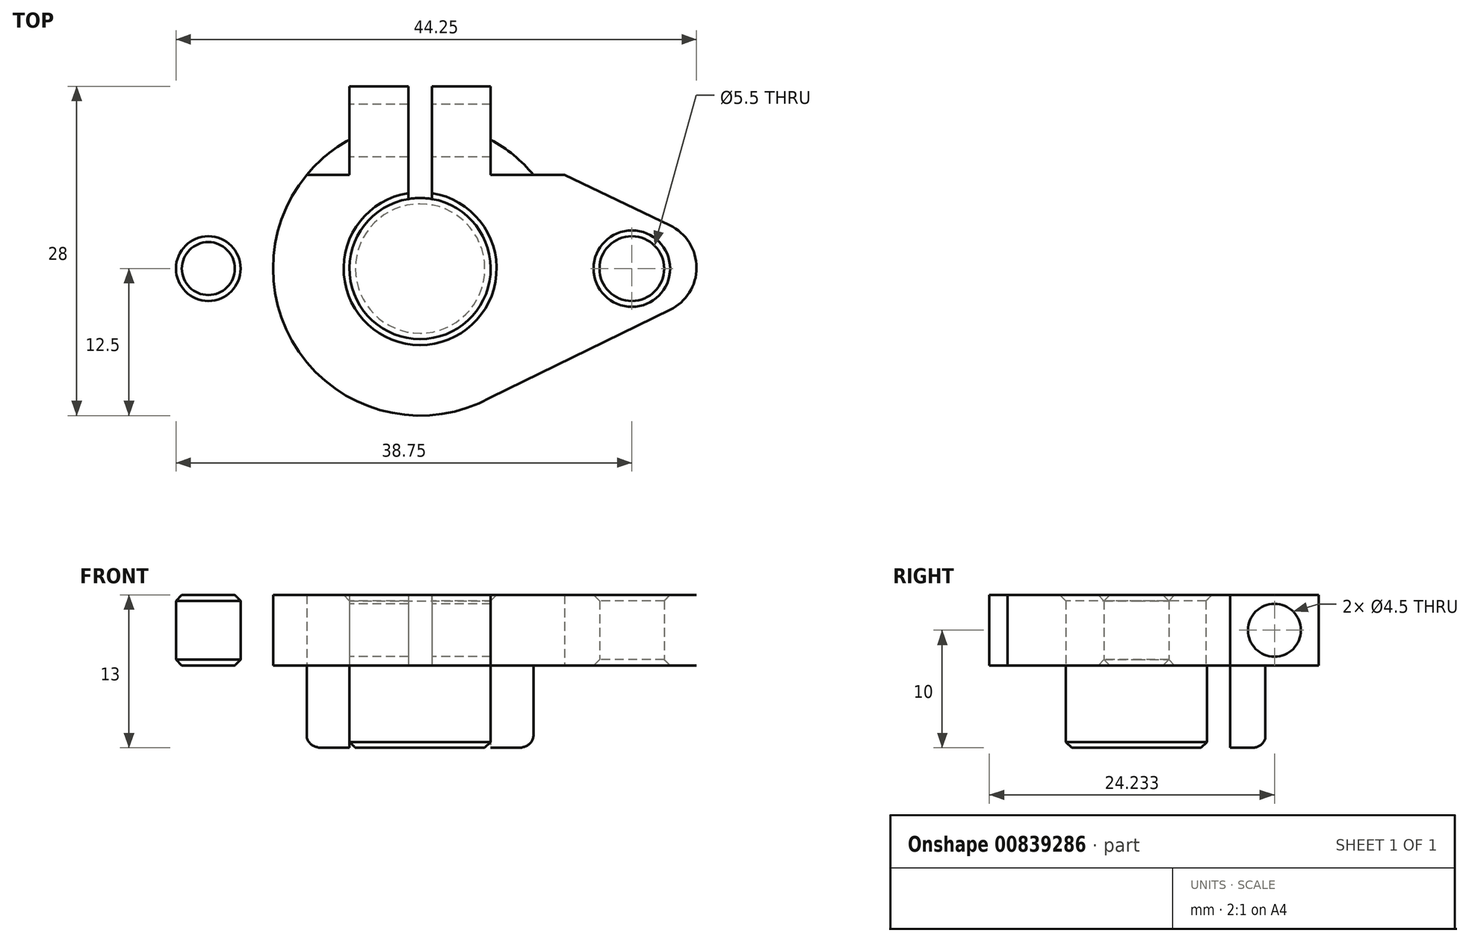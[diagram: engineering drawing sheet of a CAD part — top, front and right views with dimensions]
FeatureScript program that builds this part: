
annotation { "Feature Type Name" : "Feature", "Feature Type Description" : "" }
export const myFeature = defineFeature(function(context is Context, id is Id, definition is map)
    precondition{}
    {
        {
            var Q0;
            Q0=qCreatedBy(makeId("Top.planeOp"),FACE);
            var sketch = newSketch(context, id + "F0", { "sketchPlane" : qUnion([Q0])});
            skCircle(sketch, "E0", {"center": v(0, 0) * mm, "radius": 6 * mm});
            skCircle(sketch, "E1", {"center": v(0, 0) * mm, "radius": 12.5 * mm});
            skCircle(sketch, "E2", {"center": v(18, 0) * mm, "radius": 2.75 * mm});
            skCircle(sketch, "E3.MirrorC", {"center": v(-18, 0) * mm, "radius": 2.75 * mm});
            skLineSegment(sketch, "E4", {"start": v(-1, 5.92) * mm, "end": v(-1, 15.5) * mm});
            skLineSegment(sketch, "E5.MirrorCS", {"start": v(1, 5.92) * mm, "end": v(1, 15.5) * mm});
            skLineSegment(sketch, "E6", {"start": v(-1, 15.5) * mm, "end": v(1, 15.5) * mm});
            skPoint(sketch, "E7", {"position": v(0, -12.5) * mm});
            skLineSegment(sketch, "E8", {"start": v(1, 15.5) * mm, "end": v(6, 15.5) * mm});
            skLineSegment(sketch, "E9", {"start": v(6, 15.5) * mm, "end": v(6, 10.97) * mm});
            skLineSegment(sketch, "E10.MirrorCS", {"start": v(-1, 15.5) * mm, "end": v(-6, 15.5) * mm});
            skLineSegment(sketch, "E11.MirrorCS", {"start": v(-6, 15.5) * mm, "end": v(-6, 10.97) * mm});
            skLineSegment(sketch, "E12", {"start": v(23.5, -2.4) * mm, "end": v(23.5, 2.6) * mm});
            skLineSegment(sketch, "E13.MirrorCS", {"start": v(-23.5, -2.4) * mm, "end": v(-23.5, 2.6) * mm});
            skLineSegment(sketch, "E14", {"start": v(-6, 10.97) * mm, "end": v(-23.5, 2.6) * mm});
            skLineSegment(sketch, "E15", {"start": v(-23.5, -2.4) * mm, "end": v(-6, -10.97) * mm});
            skLineSegment(sketch, "E16", {"start": v(6, -10.97) * mm, "end": v(23.5, -2.4) * mm});
            skLineSegment(sketch, "E17", {"start": v(23.5, 2.6) * mm, "end": v(6, 10.97) * mm});
            skLineSegment(sketch, "E18", {"start": v(6, 10.97) * mm, "end": v(6, 7.97) * mm});
            skLineSegment(sketch, "E19", {"start": v(6, 7.97) * mm, "end": v(12.27, 7.97) * mm});
            skLineSegment(sketch, "E20.MirrorCS", {"start": v(-6, 10.97) * mm, "end": v(-6, 7.97) * mm});
            skLineSegment(sketch, "E21.MirrorCS", {"start": v(-6, 7.97) * mm, "end": v(-12.27, 7.97) * mm});
            skSolve(sketch);
        }
        {
            var Q0;
            Q0=makeQuery(id+"F0.imprint","IMPRINT",FACE,{"disambiguationData":[TD([[makeQuery(id+"F0.imprint","IMPRINT",EDGE,{"derivedFrom":sQuery(id+"F0.wireOp",EDGE,"E3.MirrorC")}),1.0]])]});
            var Q1;
            {var subQ5=sQuery(id+"F0.wireOp",EDGE,"E18");Q1=makeQuery(id+"F0.imprint","IMPRINT",FACE,{"disambiguationData":[TD([[makeQuery(id+"F0.imprint","IMPRINT",EDGE,{"derivedFrom":subQ5}),-1.0]])]});}
            var Q2;
            Q2=makeQuery(id+"F0.imprint","IMPRINT",FACE,{"disambiguationData":[TD([[makeQuery(id+"F0.imprint","IMPRINT",EDGE,{"derivedFrom":sQuery(id+"F0.wireOp",EDGE,"E2")}),-1.0]])]});
            var Q3;
            {var subQ4=sQuery(id+"F0.wireOp",EDGE,"E10.MirrorCS");Q3=makeQuery(id+"F0.imprint","IMPRINT",FACE,{"disambiguationData":[TD([[makeQuery(id+"F0.imprint","IMPRINT",EDGE,{"derivedFrom":subQ4}),1.0]])]});}
            var Q4;
            {var subQ4=sQuery(id+"F0.wireOp",EDGE,"E8");Q4=makeQuery(id+"F0.imprint","IMPRINT",FACE,{"disambiguationData":[TD([[makeQuery(id+"F0.imprint","IMPRINT",EDGE,{"derivedFrom":subQ4}),-1.0]])]});}
            extrude(context, id + "F1", {"entities" : qUnion([Q0, Q1, Q2, Q3, Q4]), "depth" : 6 * mm, "offsetDistance" : 25 * mm});
        }
        {
            var Q0;
            Q0=makeQuery(id+"F1.opExtrude","SWEPT_FACE",FACE,{"disambiguationData":[OSD([sQuery(id+"F0.wireOp",EDGE,"E11.MirrorCS"),sQuery(id+"F0.wireOp",EDGE,"E20.MirrorCS")])]});
            var sketch = newSketch(context, id + "F2", { "sketchPlane" : qUnion([Q0])});
            skLineSegment(sketch, "E22", {"start": v(-15.5, 3) * mm, "end": v(-7.97, 3) * mm});
            skPoint(sketch, "E23", {"position": v(-11.73, 3) * mm});
            skSolve(sketch);
        }
        {
            var Q0;
            Q0=sQuery(id+"F2.wireOp",VERTEX,"E23");
            var Q1;
            Q1=makeQuery(id+"F1.opExtrude","SWEPT_BODY",BODY,{"disambiguationData":[OSD([sQuery(id+"F0.wireOp",EDGE,"E0"),sQuery(id+"F0.wireOp",EDGE,"E1"),sQuery(id+"F0.wireOp",EDGE,"E2"),sQuery(id+"F0.wireOp",EDGE,"E3.MirrorC"),sQuery(id+"F0.wireOp",EDGE,"E4"),sQuery(id+"F0.wireOp",EDGE,"E5.MirrorCS"),sQuery(id+"F0.wireOp",EDGE,"E8"),sQuery(id+"F0.wireOp",EDGE,"E9"),sQuery(id+"F0.wireOp",EDGE,"E10.MirrorCS"),sQuery(id+"F0.wireOp",EDGE,"E11.MirrorCS"),sQuery(id+"F0.wireOp",EDGE,"E12"),sQuery(id+"F0.wireOp",EDGE,"E13.MirrorCS"),sQuery(id+"F0.wireOp",EDGE,"E14"),sQuery(id+"F0.wireOp",EDGE,"E15"),sQuery(id+"F0.wireOp",EDGE,"E16"),sQuery(id+"F0.wireOp",EDGE,"E17"),sQuery(id+"F0.wireOp",EDGE,"E18"),sQuery(id+"F0.wireOp",EDGE,"E19"),sQuery(id+"F0.wireOp",EDGE,"E20.MirrorCS"),sQuery(id+"F0.wireOp",EDGE,"E21.MirrorCS")])]});
            hole(context, id + "F3", {"style" : HoleStyle.SIMPLE, "endStyle" : HoleEndStyle.THROUGH, "standardTappedOrClearance" : lookupTablePath({ "fit" : "Normal", "standard" : "ISO", "size" : "M4", "type" : "Clearance" }), "standardBlindInLast" : lookupTablePath({ "fit" : "Normal", "standard" : "ISO", "engagement" : "75%", "pitch" : "0.7 mm", "size" : "M4", "type" : "Clearance & tapped" }), "holeDiameter" : 4.5 * mm, "majorDiameter" : 3 * mm, "isTappedThrough" : true, "tappedDepth" : 10 * mm, "tapClearance" : 3, "locations" : qUnion([Q0]), "scope" : qUnion([Q1])});
        }
        {
            var Q0;
            Q0=makeQuery(id+"F1.opExtrude","CAP_FACE",FACE,{"disambiguationData":[OSD([sQuery(id+"F0.wireOp",EDGE,"E0"),sQuery(id+"F0.wireOp",EDGE,"E1"),sQuery(id+"F0.wireOp",EDGE,"E2"),sQuery(id+"F0.wireOp",EDGE,"E3.MirrorC"),sQuery(id+"F0.wireOp",EDGE,"E4"),sQuery(id+"F0.wireOp",EDGE,"E5.MirrorCS"),sQuery(id+"F0.wireOp",EDGE,"E8"),sQuery(id+"F0.wireOp",EDGE,"E9"),sQuery(id+"F0.wireOp",EDGE,"E10.MirrorCS"),sQuery(id+"F0.wireOp",EDGE,"E11.MirrorCS"),sQuery(id+"F0.wireOp",EDGE,"E12"),sQuery(id+"F0.wireOp",EDGE,"E13.MirrorCS"),sQuery(id+"F0.wireOp",EDGE,"E14"),sQuery(id+"F0.wireOp",EDGE,"E15"),sQuery(id+"F0.wireOp",EDGE,"E16"),sQuery(id+"F0.wireOp",EDGE,"E17"),sQuery(id+"F0.wireOp",EDGE,"E18"),sQuery(id+"F0.wireOp",EDGE,"E19"),sQuery(id+"F0.wireOp",EDGE,"E20.MirrorCS"),sQuery(id+"F0.wireOp",EDGE,"E21.MirrorCS")])],"isStart":true});
            var sketch = newSketch(context, id + "F4", { "sketchPlane" : qUnion([Q0])});
            skCircle(sketch, "E24", {"center": v(0, 0) * mm, "radius": 6 * mm});
            skCircle(sketch, "E25", {"center": v(0, 0) * mm, "radius": 12.5 * mm});
            skLineSegment(sketch, "E26", {"start": v(1, -5.92) * mm, "end": v(1, -12.46) * mm});
            skLineSegment(sketch, "E27", {"start": v(-1, -5.92) * mm, "end": v(-1, -12.46) * mm});
            skSolve(sketch);
        }
        {
            var Q0;
            Q0=makeQuery(id+"F4.imprint","IMPRINT",FACE,{"disambiguationData":[TD([[makeQuery(id+"F4.imprint","IMPRINT",EDGE,{"disambiguationData":[OD(0.0)],"derivedFrom":sQuery(id+"F4.wireOp",EDGE,"E24")}),1.0]])]});
            var Q1;
            {var subQ0=sQuery(id+"F4.wireOp",EDGE,"E25");var subQ1=makeQuery(id+"F1.opExtrude","CAP_EDGE",EDGE,{"disambiguationData":[OSD([sQuery(id+"F0.wireOp",EDGE,"E9"),sQuery(id+"F0.wireOp",EDGE,"E18")])],"isStart":true});var subQ2=makeQuery(id+"F4.imprint","INTERSECT",VERTEX,{"derivedFrom":[subQ1,subQ0]});var subQ3=makeQuery(id+"F1.opExtrude","CAP_EDGE",EDGE,{"disambiguationData":[OSD([sQuery(id+"F0.wireOp",EDGE,"E19")])],"isStart":true});var subQ4=makeQuery(id+"F4.imprint","INTERSECT",VERTEX,{"derivedFrom":[subQ3,subQ0]});Q1=makeQuery(id+"F4.imprint","IMPRINT",FACE,{"disambiguationData":[TD([[makeQuery(id+"F4.imprint","IMPRINT",EDGE,{"disambiguationData":[TD([[subQ2,-1.0],[subQ4,1.0]])],"derivedFrom":subQ0}),1.0]])]});}
            var Q2;
            {var subQ0=sQuery(id+"F4.wireOp",EDGE,"E25");var subQ1=makeQuery(id+"F1.opExtrude","CAP_EDGE",EDGE,{"disambiguationData":[OSD([sQuery(id+"F0.wireOp",EDGE,"E21.MirrorCS")])],"isStart":true});var subQ2=makeQuery(id+"F4.imprint","INTERSECT",VERTEX,{"derivedFrom":[subQ1,subQ0]});var subQ3=makeQuery(id+"F1.opExtrude","CAP_EDGE",EDGE,{"disambiguationData":[OSD([sQuery(id+"F0.wireOp",EDGE,"E11.MirrorCS"),sQuery(id+"F0.wireOp",EDGE,"E20.MirrorCS")])],"isStart":true});var subQ4=makeQuery(id+"F4.imprint","INTERSECT",VERTEX,{"derivedFrom":[subQ3,subQ0]});Q2=makeQuery(id+"F4.imprint","IMPRINT",FACE,{"disambiguationData":[TD([[makeQuery(id+"F4.imprint","IMPRINT",EDGE,{"disambiguationData":[TD([[subQ2,-1.0],[subQ4,1.0]])],"derivedFrom":subQ0}),1.0]])]});}
            extrude(context, id + "F5", {"entities" : qUnion([Q0, Q1, Q2]), "operationType" : NewBodyOperationType.ADD, "depth" : 7 * mm, "offsetDistance" : 25 * mm});
        }
        {
            var Q0;
            Q0=makeQuery(id+"F5.opExtrude","CAP_EDGE",EDGE,{"disambiguationData":[OSD([sQuery(id+"F4.wireOp",EDGE,"E25")])],"isStart":false});
            fillet(context, id + "F6", {"entities" : qUnion([Q0]), "radius" : 1 * mm, "tangentPropagation" : true, "allowEdgeOverflow" : false});
        }
        {
            var Q0;
            Q0=makeQuery(id+"F5.opExtrude","CAP_EDGE",EDGE,{"disambiguationData":[OSD([sQuery(id+"F4.wireOp",EDGE,"E24")])],"isStart":false});
            var Q1;
            Q1=makeQuery(id+"F1.opExtrude","CAP_EDGE",EDGE,{"disambiguationData":[OSD([sQuery(id+"F0.wireOp",EDGE,"E0")])],"isStart":false});
            var Q2;
            Q2=makeQuery(id+"F1.opExtrude","CAP_EDGE",EDGE,{"disambiguationData":[OSD([sQuery(id+"F0.wireOp",EDGE,"E2")])],"isStart":true});
            var Q3;
            Q3=makeQuery(id+"F1.opExtrude","CAP_EDGE",EDGE,{"disambiguationData":[OSD([sQuery(id+"F0.wireOp",EDGE,"E3.MirrorC")])],"isStart":true});
            var Q4;
            Q4=makeQuery(id+"F1.opExtrude","CAP_EDGE",EDGE,{"disambiguationData":[OSD([sQuery(id+"F0.wireOp",EDGE,"E2")])],"isStart":false});
            var Q5;
            Q5=makeQuery(id+"F1.opExtrude","CAP_EDGE",EDGE,{"disambiguationData":[OSD([sQuery(id+"F0.wireOp",EDGE,"E3.MirrorC")])],"isStart":false});
            var Q6;
            Q6=makeQuery(id+"F3.hole-0.boolean.opBoolean","INTERSECT",EDGE,{"derivedFrom":[makeQuery(id+"F1.opExtrude","SWEPT_FACE",FACE,{"disambiguationData":[OSD([sQuery(id+"F0.wireOp",EDGE,"E9"),sQuery(id+"F0.wireOp",EDGE,"E18")])]}),makeQuery(id+"F3.hole-0.opRevolve","SWEPT_FACE",FACE,{"disambiguationData":[OSD([sQuery(id+"F3.hole-0.sketch.wireOp",EDGE,"core_line_2")])]})]});
            var Q7;
            Q7=makeQuery(id+"F3.hole-0.boolean.opBoolean","COPY",EDGE,{"derivedFrom":makeQuery(id+"F3.hole-0.opRevolve","SWEPT_EDGE",EDGE,{"disambiguationData":[OSD([sQuery(id+"F3.hole-0.sketch.wireOp",EDGE,"core_line_2"),sQuery(id+"F3.hole-0.sketch.wireOp",EDGE,"core_line_3")])]})});
            chamfer(context, id + "F7", {"entities" : qUnion([Q0, Q1, Q2, Q3, Q4, Q5, Q6, Q7]), "width" : 0.5 * mm, "tangentPropagation" : true});
        }
        {
            var Q0;
            Q0=makeQuery(id+"F1.opExtrude","SWEPT_EDGE",EDGE,{"disambiguationData":[OSD([sQuery(id+"F0.wireOp",EDGE,"E13.MirrorCS"),sQuery(id+"F0.wireOp",EDGE,"E14")])]});
            var Q1;
            Q1=makeQuery(id+"F1.opExtrude","SWEPT_EDGE",EDGE,{"disambiguationData":[OSD([sQuery(id+"F0.wireOp",EDGE,"E13.MirrorCS"),sQuery(id+"F0.wireOp",EDGE,"E15")])]});
            var Q2;
            Q2=makeQuery(id+"F1.opExtrude","SWEPT_EDGE",EDGE,{"disambiguationData":[OSD([sQuery(id+"F0.wireOp",EDGE,"E12"),sQuery(id+"F0.wireOp",EDGE,"E17")])]});
            var Q3;
            Q3=makeQuery(id+"F1.opExtrude","SWEPT_EDGE",EDGE,{"disambiguationData":[OSD([sQuery(id+"F0.wireOp",EDGE,"E12"),sQuery(id+"F0.wireOp",EDGE,"E16")])]});
            fillet(context, id + "F8", {"entities" : qUnion([Q0, Q1, Q2, Q3]), "radius" : 4 * mm, "tangentPropagation" : true, "allowEdgeOverflow" : false});
        }
    });
